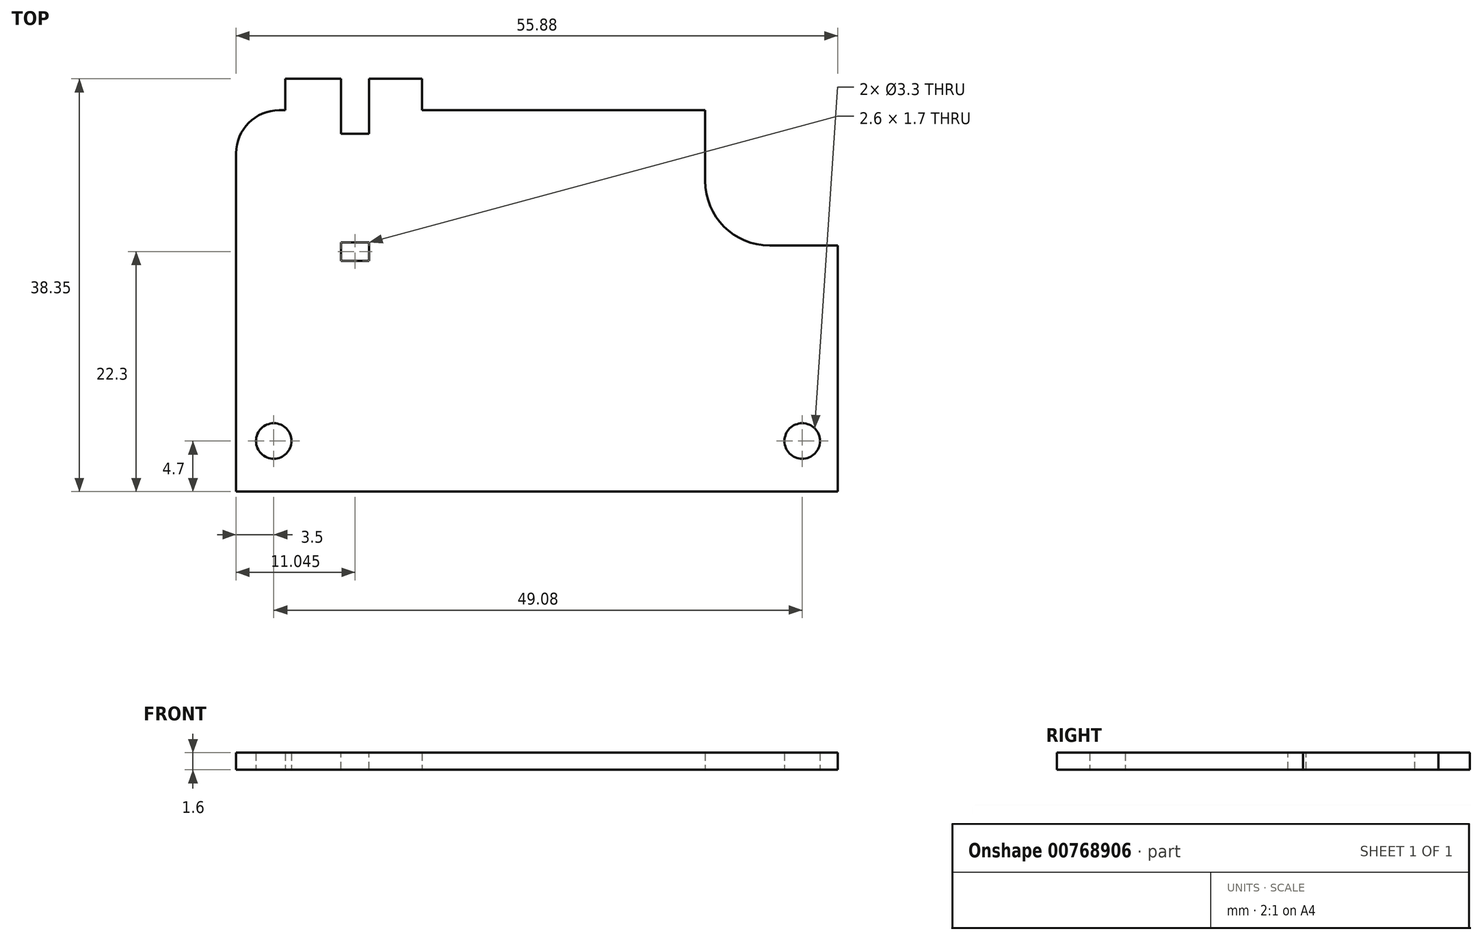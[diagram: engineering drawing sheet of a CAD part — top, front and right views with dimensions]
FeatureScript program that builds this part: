
annotation { "Feature Type Name" : "Feature", "Feature Type Description" : "" }
export const myFeature = defineFeature(function(context is Context, id is Id, definition is map)
    precondition{}
    {
        {
            var Q0;
            Q0=qCreatedBy(makeId("Top.planeOp"),FACE);
            var sketch = newSketch(context, id + "F0", { "sketchPlane" : qUnion([Q0])});
            skLineSegment(sketch, "E0", {"start": v(0, 0) * mm, "end": v(0, 35.43) * mm});
            skLineSegment(sketch, "E1", {"start": v(0, 35.43) * mm, "end": v(4.57, 35.43) * mm});
            skLineSegment(sketch, "E2", {"start": v(4.57, 35.43) * mm, "end": v(4.57, 38.35) * mm});
            skLineSegment(sketch, "E3", {"start": v(4.57, 38.35) * mm, "end": v(17.27, 38.35) * mm});
            skLineSegment(sketch, "E4", {"start": v(17.27, 38.35) * mm, "end": v(17.27, 35.43) * mm});
            skLineSegment(sketch, "E5", {"start": v(17.27, 35.43) * mm, "end": v(43.56, 35.43) * mm});
            skCircle(sketch, "E6", {"center": v(3.5, 4.7) * mm, "radius": 1.65 * mm});
            skLineSegment(sketch, "E7", {"start": v(43.56, 35.43) * mm, "end": v(43.56, 22.86) * mm});
            skLineSegment(sketch, "E8", {"start": v(43.56, 22.86) * mm, "end": v(55.88, 22.86) * mm});
            skLineSegment(sketch, "E9", {"start": v(55.88, 22.86) * mm, "end": v(55.88, 0) * mm});
            skLineSegment(sketch, "E10", {"start": v(55.88, 0) * mm, "end": v(0, 0) * mm});
            skCircle(sketch, "E11", {"center": v(52.58, 4.7) * mm, "radius": 1.65 * mm});
            skLineSegment(sketch, "E12", {"start": v(4.57, 35.43) * mm, "end": v(17.27, 35.43) * mm, "construction": true});
            skLineSegment(sketch, "E13", {"start": v(3.5, 4.7) * mm, "end": v(52.58, 4.7) * mm, "construction": true});
            skSolve(sketch);
        }
        {
            var Q0;
            Q0=qSketchRegion(id+"F0",true);
            extrude(context, id + "F1", {"entities" : qUnion([Q0]), "depth" : 1.6 * mm, "offsetDistance" : 25 * mm});
        }
        {
            var Q0;
            Q0=makeQuery(id+"F1.opExtrude","SWEPT_EDGE",EDGE,{"disambiguationData":[OSD([sQuery(id+"F0.wireOp",EDGE,"E0"),sQuery(id+"F0.wireOp",EDGE,"E1")])]});
            fillet(context, id + "F2", {"entities" : qUnion([Q0]), "radius" : 4 * mm, "tangentPropagation" : true, "allowEdgeOverflow" : false});
        }
        {
            var Q0;
            Q0=makeQuery(id+"F1.opExtrude","SWEPT_EDGE",EDGE,{"disambiguationData":[OSD([sQuery(id+"F0.wireOp",EDGE,"E7"),sQuery(id+"F0.wireOp",EDGE,"E8")])]});
            fillet(context, id + "F3", {"entities" : qUnion([Q0]), "radius" : 6 * mm, "tangentPropagation" : true, "allowEdgeOverflow" : false});
        }
        {
            var Q0;
            Q0=makeQuery(id+"F1.opExtrude","CAP_FACE",FACE,{"disambiguationData":[OSD([sQuery(id+"F0.wireOp",EDGE,"E0"),sQuery(id+"F0.wireOp",EDGE,"E1"),sQuery(id+"F0.wireOp",EDGE,"E2"),sQuery(id+"F0.wireOp",EDGE,"E3"),sQuery(id+"F0.wireOp",EDGE,"E4"),sQuery(id+"F0.wireOp",EDGE,"E5"),sQuery(id+"F0.wireOp",EDGE,"E6"),sQuery(id+"F0.wireOp",EDGE,"E7"),sQuery(id+"F0.wireOp",EDGE,"E8"),sQuery(id+"F0.wireOp",EDGE,"E9"),sQuery(id+"F0.wireOp",EDGE,"E10"),sQuery(id+"F0.wireOp",EDGE,"E11")])],"isStart":false});
            var sketch = newSketch(context, id + "F4", { "sketchPlane" : qUnion([Q0])});
            skLineSegment(sketch, "E14.bottom", {"start": v(6.84, 38.35) * mm, "end": v(4.25, 38.35) * mm, "construction": true});
            skLineSegment(sketch, "E14.top", {"start": v(6.85, 33.25) * mm, "end": v(4.25, 33.25) * mm, "construction": true});
            skLineSegment(sketch, "E14.left", {"start": v(6.84, 38.35) * mm, "end": v(6.84, 33.25) * mm, "construction": true});
            skLineSegment(sketch, "E14.right", {"start": v(4.25, 38.35) * mm, "end": v(4.25, 33.25) * mm, "construction": true});
            skLineSegment(sketch, "E15.bottom", {"start": v(9.75, 38.35) * mm, "end": v(12.34, 38.35) * mm});
            skLineSegment(sketch, "E15.top", {"start": v(9.75, 33.25) * mm, "end": v(12.35, 33.25) * mm});
            skLineSegment(sketch, "E15.left", {"start": v(9.75, 38.35) * mm, "end": v(9.75, 33.25) * mm});
            skLineSegment(sketch, "E15.right", {"start": v(12.35, 38.35) * mm, "end": v(12.35, 33.25) * mm});
            skLineSegment(sketch, "E16.bottom", {"start": v(4.25, 23.15) * mm, "end": v(6.85, 23.15) * mm, "construction": true});
            skLineSegment(sketch, "E16.top", {"start": v(4.25, 21.45) * mm, "end": v(6.85, 21.45) * mm, "construction": true});
            skLineSegment(sketch, "E16.left", {"start": v(4.25, 23.15) * mm, "end": v(4.25, 21.45) * mm, "construction": true});
            skLineSegment(sketch, "E16.right", {"start": v(6.84, 23.15) * mm, "end": v(6.84, 21.45) * mm, "construction": true});
            skLineSegment(sketch, "E17.bottom", {"start": v(9.75, 23.15) * mm, "end": v(12.35, 23.15) * mm});
            skLineSegment(sketch, "E17.top", {"start": v(9.75, 21.45) * mm, "end": v(12.35, 21.45) * mm});
            skLineSegment(sketch, "E17.left", {"start": v(9.75, 23.15) * mm, "end": v(9.75, 21.45) * mm});
            skLineSegment(sketch, "E17.right", {"start": v(12.35, 23.15) * mm, "end": v(12.35, 21.45) * mm});
            skLineSegment(sketch, "E18", {"start": v(4.25, 23.15) * mm, "end": v(4.25, 33.25) * mm, "construction": true});
            skLineSegment(sketch, "E19", {"start": v(6.84, 23.15) * mm, "end": v(6.84, 33.25) * mm, "construction": true});
            skLineSegment(sketch, "E20", {"start": v(9.75, 23.15) * mm, "end": v(9.75, 33.25) * mm, "construction": true});
            skLineSegment(sketch, "E21", {"start": v(12.35, 23.15) * mm, "end": v(12.35, 33.25) * mm, "construction": true});
            skSolve(sketch);
        }
        {
            var Q0;
            Q0=qSketchRegion(id+"F4",true);
            extrude(context, id + "F5", {"entities" : qUnion([Q0]), "operationType" : NewBodyOperationType.REMOVE, "endBound" : BoundingType.THROUGH_ALL, "oppositeDirection" : true, "depth" : 25 * mm, "offsetDistance" : 25 * mm});
        }
    });
